# Revit family: Festpunkt Typ A Größe II, U-Stahl, Ø133-160, V2A
name_source: partatom
category: HLS-Bauteile
revit_build: Autodesk Revit 2017 (Build: 20190507_1515(x64)
units: mm (PartAtom-declared; Revit-internal decimal feet)

## family parameters
Arbeitsebenenbasiert = Ja
Beim Laden mit Abzugskörper schneiden = Nein
Bemaßung runder Anschluss = Durchmesser verwenden
Gemeinsam genutzt = Ja
Immer vertikal = Nein
Raumberechnungspunkt = Nein
Teiletyp = Normal

## types (6) — shared parameters
Anzahl Rohrschellen = 2
Aufbaumaß = 63 mm
Ausführung = mit Schweißnase
Baustoffklasse = B2
Breite Material Rohrschelle = 50 mm
Breite Profilstahl = 80 mm
Fabrikat = MEFA
Firma = MEFA Befestigungs- und Montagesysteme GmbH
Höhe Profilstahl = 45 mm
Klammergröße = 2
Kurztext1 = Festpunkt Typ A V2A
Länge Druckstück = 116 mm
Länge Profilstahl = 200 mm  [stored 0.656168 ft]
Material Druckstücke = Edelstahl
Materialname Druckstücke = V2A
Mengeneinheit = St
Oberfläche Träger + Schellen = galvanisch verzinkt
Profilstahltyp = U80
Rohrschellentyp = Titan HD
Stärke Material Rohrschelle = 5 mm
Vorgabe-Ansicht = 1219 mm
vpe = 1 St
zero-valued in all types: max. Rohraußendurchmesser, min. Rohraußendurchmesser

## per-type parameters (varying)
| type | Artikelnummer | Breite | Druckstück Typ II | EAN | Gewicht | Gewicht pro Bauteil | Kurztext2 | Material Schalldämmeinlage | RA | Rohraußendurchmesser | Rohrschellen | Schalldämmeinlage | max. Axiale Reaktionskraft | max. Höhe | max. Temperaturbeständigkeit |
| Festpunkt Typ A Größe II, Ø133, Gummi, V2A | 9999359 | 223 mm  [stored 0.731627 ft] | Druckstück Typ II Gummi für Edelstahl : Druckstück Typ II Gummi | 4250928447104 | 6.21 kg | 6.21 kg | 133 mm Gummi mit Schweißnase | TPE | 114 mm | 133 mm  [stored 0.436352 ft] | MEFA RS Titan HD, Ø60,3-Ø160 mm, TPE : MEFA RS Titan HD, Ø133 mm, TPE | Gummi |  | 0 mm  [stored 0 ft] | 100 °C |
| Festpunkt Typ A Größe II, Ø139,7, Gummi, V2A | 9999429 | 230 mm  [stored 0.754593 ft] | Druckstück Typ II Gummi für Edelstahl : Druckstück Typ II Gummi | 4250928447500 | 6.32 kg | 6.32 kg | 139.7 mm Gummi mit Schweißnase | TPE | 118 mm | 140 mm  [stored 0.459318 ft] | MEFA RS Titan HD, Ø60,3-Ø160 mm, TPE : MEFA RS Titan HD, Ø139,7 mm, TPE | Gummi |  | 0 mm  [stored 0 ft] | 100 °C |
| Festpunkt Typ A Größe II, Ø159-160, Gummi, V2A | 9999360 | 250 mm  [stored 0.82021 ft] | Druckstück Typ II Gummi für Edelstahl : Druckstück Typ II Gummi | 4250928447111 | 6.60 kg | 6.60 kg | 159 mm Gummi mit Schweißnase | TPE | 129 mm | 159 mm  [stored 0.521654 ft] | MEFA RS Titan HD, Ø60,3-Ø160 mm, TPE : MEFA RS Titan HD, Ø159-Ø160 mm, TPE | Gummi | 20 kN | 219 mm  [stored 0.718504 ft] | 100 °C |
| Festpunkt Typ A Größe II, Ø133, Silikon, V2A | 9999367 | 223 mm  [stored 0.731627 ft] | Druckstück Typ II Sillikon für Edelstahl : Druckstück Typ II Silikon | 4250928447180 | 6.21 kg | 6.21 kg | 133 mm Silikon mit Schweißnase | Silikon | 114 mm | 133 mm  [stored 0.436352 ft] | MEFA RS Titan HD, Ø60,3-Ø160 mm, Silikon : MEFA RS Titan HD, Ø133 mm, Silikon | Silikon |  | 0 mm  [stored 0 ft] | 250 °C |
| Festpunkt Typ A Größe II, Ø139,7, Silikon, V2A | 9999368 | 230 mm  [stored 0.754593 ft] | Druckstück Typ II Sillikon für Edelstahl : Druckstück Typ II Silikon | 4250928447197 | 6.32 kg | 6.32 kg | 139.7 mm Silikon mit Schweißnase | Silikon | 118 mm | 140 mm  [stored 0.459318 ft] | MEFA RS Titan HD, Ø60,3-Ø160 mm, Silikon : MEFA RS Titan HD, Ø139,7 mm, Silikon | Silikon |  | 0 mm  [stored 0 ft] | 250 °C |
| Festpunkt Typ A Größe II, Ø159-160, Silikon, V2A | 9999369 | 250 mm  [stored 0.82021 ft] | Druckstück Typ II Sillikon für Edelstahl : Druckstück Typ II Silikon | 4250928447203 | 6.60 kg | 6.60 kg | 159 mm Silikon mit Schweißnase | Silikon | 129 mm | 159 mm  [stored 0.521654 ft] | MEFA RS Titan HD, Ø60,3-Ø160 mm, Silikon : MEFA RS Titan HD, Ø159-Ø160 mm, Silikon | Silikon |  | 219 mm  [stored 0.718504 ft] | 250 °C |

note: [stored X ft] marks values corroborated as IEEE doubles in the binary element streams (Revit-internal decimal feet)

## geometry (parser evidence)
native form markers: Sweep x8
no freeform markers — native parametric forms only
